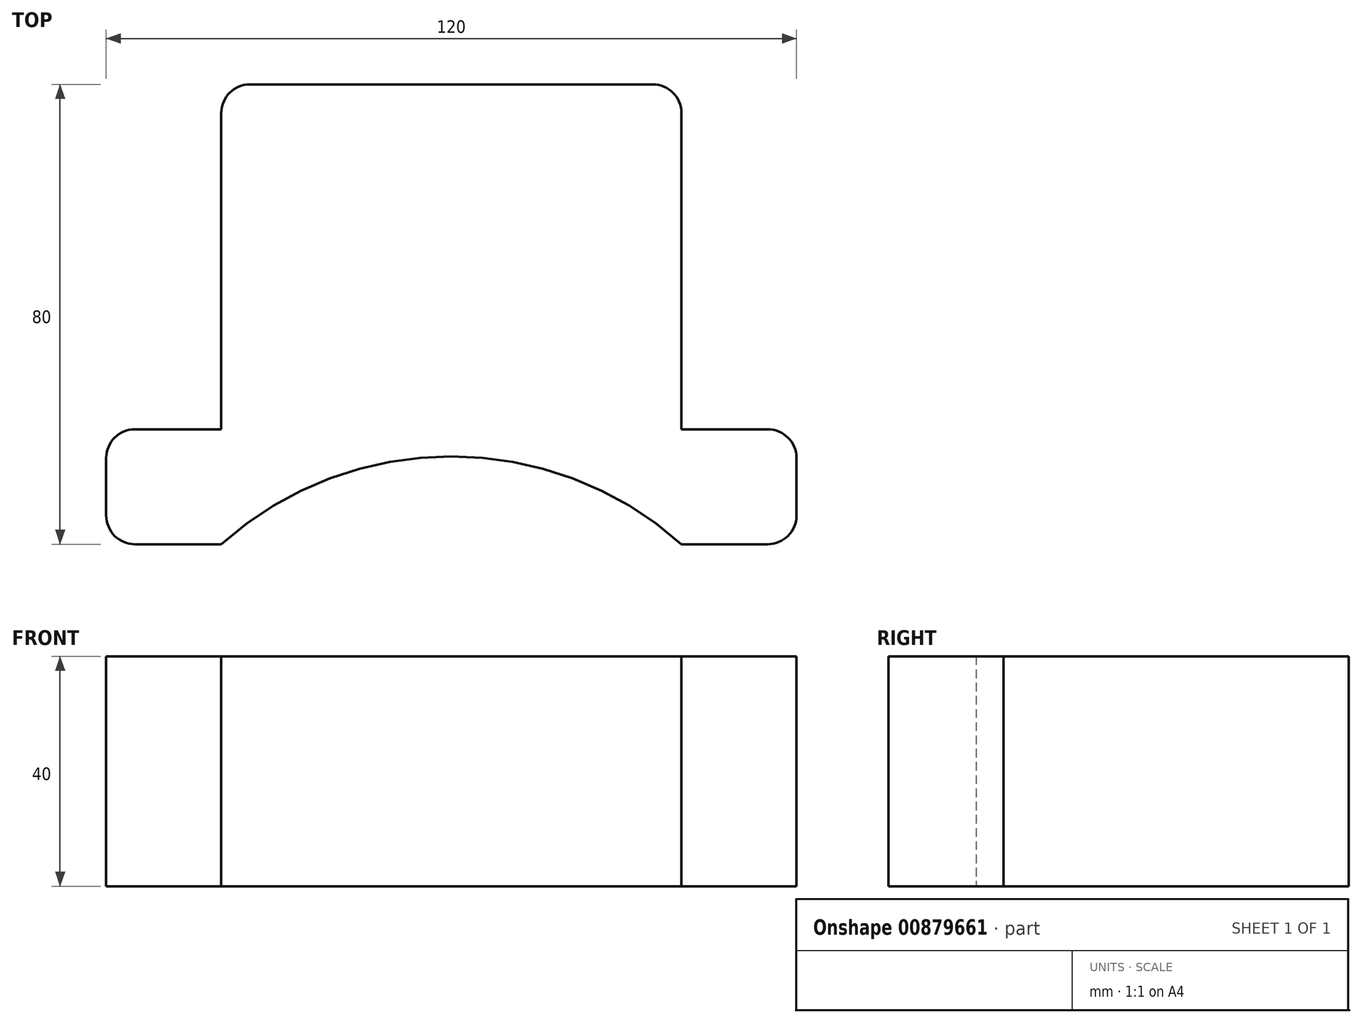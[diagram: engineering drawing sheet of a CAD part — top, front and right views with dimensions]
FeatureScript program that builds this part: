
annotation { "Feature Type Name" : "Feature", "Feature Type Description" : "" }
export const myFeature = defineFeature(function(context is Context, id is Id, definition is map)
    precondition{}
    {
        {
            var Q0;
            Q0=qCreatedBy(makeId("Top.planeOp"),FACE);
            var sketch = newSketch(context, id + "F0", { "sketchPlane" : qUnion([Q0])});
            skLineSegment(sketch, "E0.top", {"start": v(5, 80) * mm, "end": v(75, 80) * mm});
            skLineSegment(sketch, "E1.bottom", {"start": v(0, 0) * mm, "end": v(-15, 0) * mm});
            skLineSegment(sketch, "E1.top", {"start": v(0, 20) * mm, "end": v(-15, 20) * mm});
            skLineSegment(sketch, "E1.right", {"start": v(-20, 5) * mm, "end": v(-20, 15) * mm});
            skLineSegment(sketch, "E2.bottom", {"start": v(80, 0) * mm, "end": v(95, 0) * mm});
            skLineSegment(sketch, "E2.top", {"start": v(80, 20) * mm, "end": v(95, 20) * mm});
            skLineSegment(sketch, "E2.right", {"start": v(100, 5) * mm, "end": v(100, 15) * mm});
            skArc(sketch, "E3", {"start": v(80, 0) * mm, "mid": v(40, 15.26) * mm, "end": v(0, 0) * mm});
            skLineSegment(sketch, "E4", {"start": v(0, 75) * mm, "end": v(0, 20) * mm});
            skLineSegment(sketch, "E5", {"start": v(80, 75) * mm, "end": v(80, 20) * mm});
            skPoint(sketch, "E6.visualSharp", {"position": v(0, 80) * mm});
            skArc(sketch, "E6.filletArc", {"start": v(5, 80) * mm, "mid": v(1.46, 78.54) * mm, "end": v(0, 75) * mm});
            skPoint(sketch, "E7.visualSharp", {"position": v(80, 80) * mm});
            skArc(sketch, "E7.filletArc", {"start": v(80, 75) * mm, "mid": v(78.54, 78.54) * mm, "end": v(75, 80) * mm});
            skPoint(sketch, "E8.visualSharp", {"position": v(100, 20) * mm});
            skArc(sketch, "E8.filletArc", {"start": v(100, 15) * mm, "mid": v(98.54, 18.54) * mm, "end": v(95, 20) * mm});
            skPoint(sketch, "E9.visualSharp", {"position": v(100, 0) * mm});
            skArc(sketch, "E9.filletArc", {"start": v(95, 0) * mm, "mid": v(98.54, 1.46) * mm, "end": v(100, 5) * mm});
            skPoint(sketch, "E10.visualSharp", {"position": v(-20, 20) * mm});
            skArc(sketch, "E10.filletArc", {"start": v(-15, 20) * mm, "mid": v(-15.91, 19.92) * mm, "end": v(-16.8, 19.67) * mm});
            skPoint(sketch, "E11.visualSharp", {"position": v(-20, 15) * mm});
            skArc(sketch, "E11.filletArc", {"start": v(-16.8, 19.67) * mm, "mid": v(-19.12, 17.83) * mm, "end": v(-20, 15) * mm});
            skPoint(sketch, "E12.visualSharp", {"position": v(-20, 0) * mm});
            skArc(sketch, "E12.filletArc", {"start": v(-20, 5) * mm, "mid": v(-18.54, 1.46) * mm, "end": v(-15, 0) * mm});
            skSolve(sketch);
        }
        {
            var Q0;
            Q0=makeQuery(id+"F0.imprint","IMPRINT",FACE,{"disambiguationData":[TD([[makeQuery(id+"F0.imprint","IMPRINT",EDGE,{"derivedFrom":sQuery(id+"F0.wireOp",EDGE,"E0.top")}),-1.0]])]});
            extrude(context, id + "F1", {"entities" : qUnion([Q0]), "depth" : 40 * mm, "offsetDistance" : 25 * mm});
        }
    });
